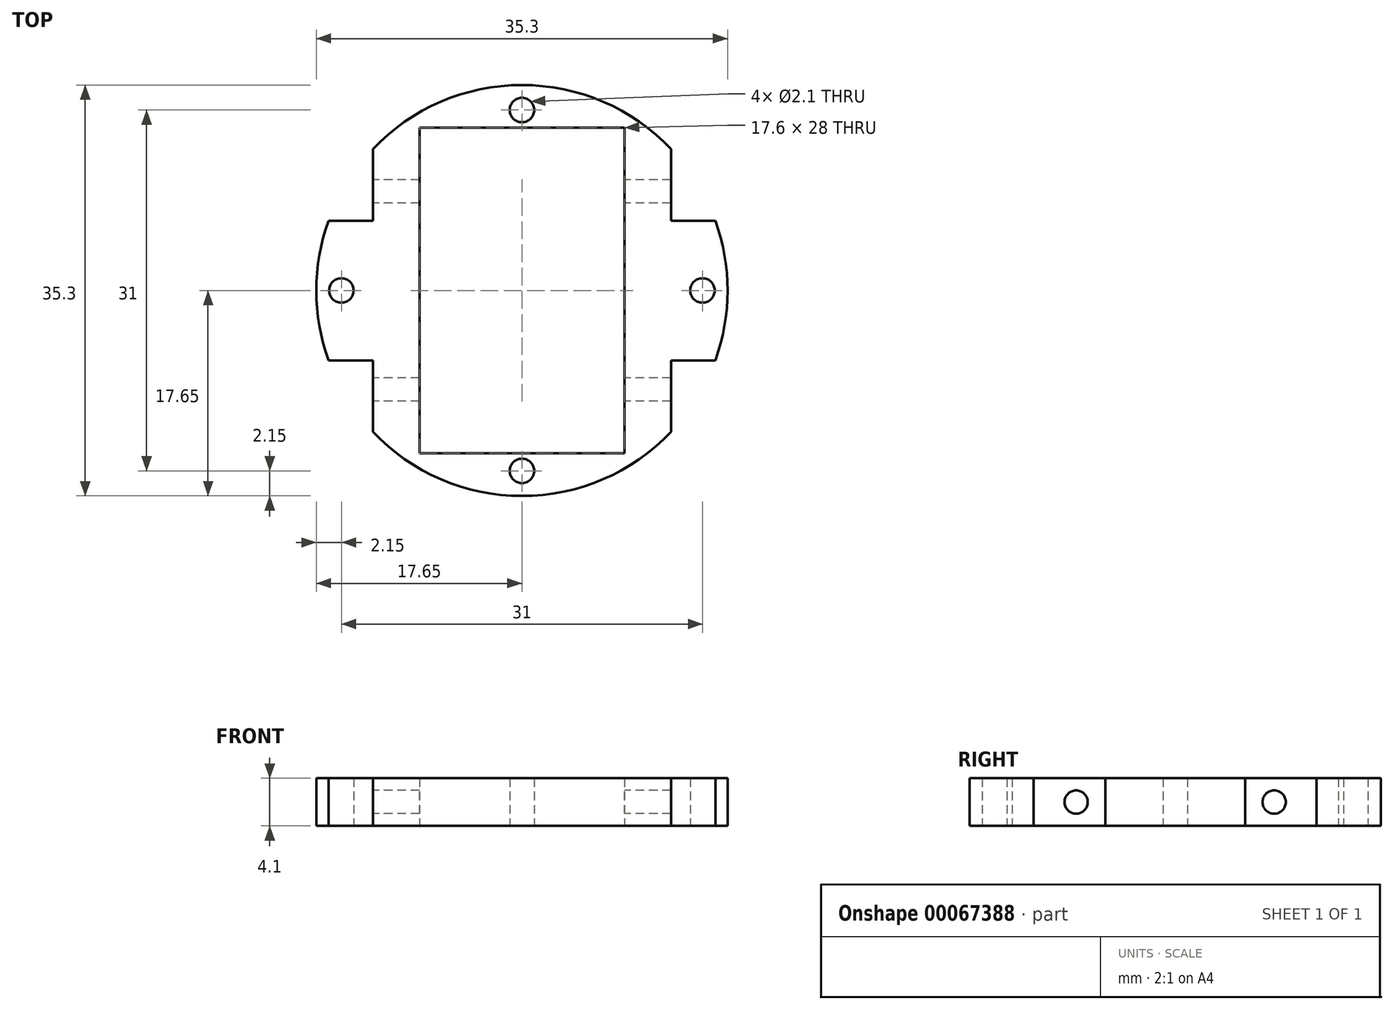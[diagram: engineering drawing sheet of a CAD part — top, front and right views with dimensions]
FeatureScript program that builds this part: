
annotation { "Feature Type Name" : "Feature", "Feature Type Description" : "" }
export const myFeature = defineFeature(function(context is Context, id is Id, definition is map)
    precondition{}
    {
        {
            var Q0;
            Q0=qCreatedBy(makeId("Top.planeOp"),FACE);
            var sketch = newSketch(context, id + "F0", { "sketchPlane" : qUnion([Q0])});
            skCircle(sketch, "E0", {"center": v(0, 0) * mm, "radius": 17.65 * mm});
            skLineSegment(sketch, "E1.bottom", {"start": v(-8.8, 14) * mm, "end": v(8.8, 14) * mm});
            skLineSegment(sketch, "E1.top", {"start": v(-8.8, -14) * mm, "end": v(8.8, -14) * mm});
            skLineSegment(sketch, "E1.left", {"start": v(-8.8, 14) * mm, "end": v(-8.8, -14) * mm});
            skLineSegment(sketch, "E1.right", {"start": v(8.8, 14) * mm, "end": v(8.8, -14) * mm});
            skCircle(sketch, "E2", {"center": v(-15.5, 0) * mm, "radius": 1.05 * mm});
            skCircle(sketch, "E3", {"center": v(15.5, 0) * mm, "radius": 1.05 * mm});
            skCircle(sketch, "E4", {"center": v(0, 15.5) * mm, "radius": 1.05 * mm});
            skCircle(sketch, "E5", {"center": v(0, -15.5) * mm, "radius": 1.05 * mm});
            skSolve(sketch);
        }
        {
            var Q0;
            Q0 = qSketchRegion(id + "F0", true);
            extrude(context, id + "F1", {"entities" : qUnion([Q0]), "depth" : 4.1 * mm});
        }
        {
            var Q0;
            Q0=makeQuery(id+"F1.opExtrude","CAP_FACE",FACE,{"disambiguationData":[OSD([sQuery(id+"F0.wireOp",EDGE,"E0"),sQuery(id+"F0.wireOp",EDGE,"E1.bottom"),sQuery(id+"F0.wireOp",EDGE,"E1.top"),sQuery(id+"F0.wireOp",EDGE,"E1.left"),sQuery(id+"F0.wireOp",EDGE,"E1.right"),sQuery(id+"F0.wireOp",EDGE,"E2"),sQuery(id+"F0.wireOp",EDGE,"E3"),sQuery(id+"F0.wireOp",EDGE,"E4"),sQuery(id+"F0.wireOp",EDGE,"E5")])],"isStart":false});
            var sketch = newSketch(context, id + "F2", { "sketchPlane" : qUnion([Q0])});
            skLineSegment(sketch, "E6.bottom", {"start": v(-12.8, 15.6) * mm, "end": v(-21.24, 15.6) * mm});
            skLineSegment(sketch, "E6.top", {"start": v(-12.8, 6) * mm, "end": v(-21.24, 6) * mm});
            skLineSegment(sketch, "E6.left", {"start": v(-12.8, 15.6) * mm, "end": v(-12.8, 6) * mm});
            skLineSegment(sketch, "E6.right", {"start": v(-21.24, 15.6) * mm, "end": v(-21.24, 6) * mm});
            skLineSegment(sketch, "E7.bottom", {"start": v(12.8, 18.1) * mm, "end": v(22.65, 18.1) * mm});
            skLineSegment(sketch, "E7.top", {"start": v(12.8, 6) * mm, "end": v(22.65, 6) * mm});
            skLineSegment(sketch, "E7.left", {"start": v(12.8, 18.1) * mm, "end": v(12.8, 6) * mm});
            skLineSegment(sketch, "E7.right", {"start": v(22.65, 18.1) * mm, "end": v(22.65, 6) * mm});
            skLineSegment(sketch, "E8.bottom", {"start": v(12.8, -6) * mm, "end": v(24.02, -6) * mm});
            skLineSegment(sketch, "E8.top", {"start": v(12.8, -18.74) * mm, "end": v(24.02, -18.74) * mm});
            skLineSegment(sketch, "E8.left", {"start": v(12.8, -6) * mm, "end": v(12.8, -18.74) * mm});
            skLineSegment(sketch, "E8.right", {"start": v(24.02, -6) * mm, "end": v(24.02, -18.74) * mm});
            skLineSegment(sketch, "E9.bottom", {"start": v(-12.8, -6) * mm, "end": v(-23.93, -6) * mm});
            skLineSegment(sketch, "E9.top", {"start": v(-12.8, -18.74) * mm, "end": v(-23.93, -18.74) * mm});
            skLineSegment(sketch, "E9.left", {"start": v(-12.8, -6) * mm, "end": v(-12.8, -18.74) * mm});
            skLineSegment(sketch, "E9.right", {"start": v(-23.93, -6) * mm, "end": v(-23.93, -18.74) * mm});
            skSolve(sketch);
        }
        {
            var Q0;
            Q0 = qSketchRegion(id + "F2", true);
            extrude(context, id + "F3", {"entities" : qUnion([Q0]), "operationType" : NewBodyOperationType.REMOVE, "endBound" : BoundingType.THROUGH_ALL, "oppositeDirection" : true, "depth" : 25 * mm});
        }
        {
            var Q0;
            Q0=makeQuery(id+"F3.boolean.opBoolean","COPY",FACE,{"derivedFrom":makeQuery(id+"F3.opExtrude","SWEPT_FACE",FACE,{"disambiguationData":[OSD([sQuery(id+"F2.wireOp",EDGE,"E6.left")])]})});
            var sketch = newSketch(context, id + "F4", { "sketchPlane" : qUnion([Q0])});
            skCircle(sketch, "E10", {"center": v(-8.5, 2.05) * mm, "radius": 1 * mm});
            skLineSegment(sketch, "E11", {"start": v(-14.7, 2.05) * mm, "end": v(20.5, 2.05) * mm, "construction": true});
            skCircle(sketch, "E12", {"center": v(8.5, 2.05) * mm, "radius": 1 * mm});
            skSolve(sketch);
        }
        {
            var Q0;
            Q0 = qSketchRegion(id + "F4", true);
            extrude(context, id + "F5", {"entities" : qUnion([Q0]), "operationType" : NewBodyOperationType.REMOVE, "endBound" : BoundingType.THROUGH_ALL, "oppositeDirection" : true, "depth" : 25 * mm});
        }
    });
